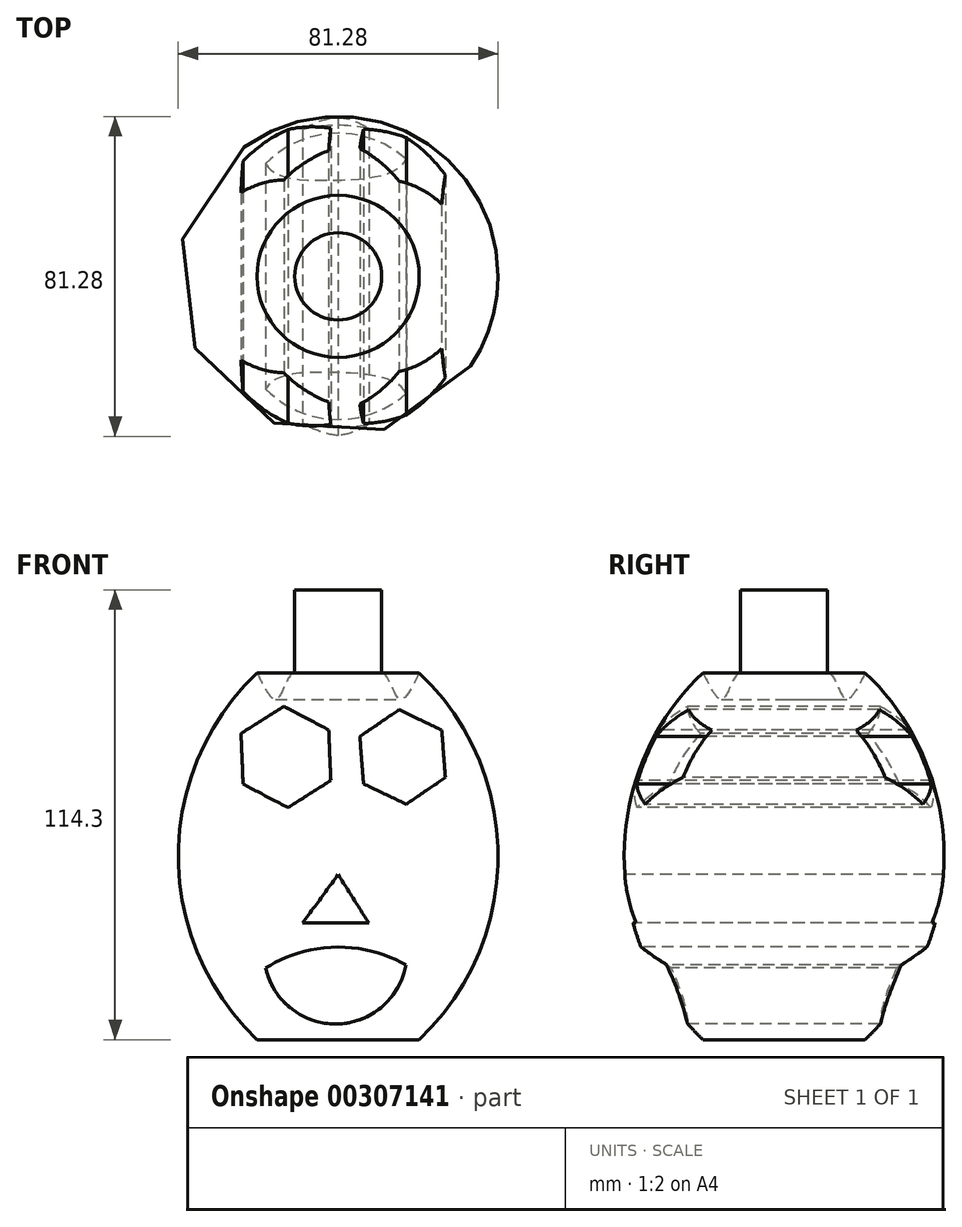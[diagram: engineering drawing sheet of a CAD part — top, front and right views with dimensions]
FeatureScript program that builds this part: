
annotation { "Feature Type Name" : "Feature", "Feature Type Description" : "" }
export const myFeature = defineFeature(function(context is Context, id is Id, definition is map)
    precondition{}
    {
        {
            var Q0;
            Q0=qCreatedBy(makeId("Front.planeOp"),FACE);
            var sketch = newSketch(context, id + "F0", { "sketchPlane" : qUnion([Q0])});
            skLineSegment(sketch, "E0", {"start": v(0, 0) * mm, "end": v(20.6, 0) * mm});
            skArc(sketch, "E1", {"start": v(20.6, 0) * mm, "mid": v(40.64, 46.6) * mm, "end": v(20.6, 93.21) * mm});
            skFitSpline(sketch, "E2", {"points": [v(20.6, 93.21) * mm, v(15.47, 86.64) * mm, v(11.1, 93.21) * mm, v(3.47, 86.37) * mm, v(0, 89.37) * mm], "startDerivative": vector(-21.04, -43.12) * mm, "endDerivative": vector(-15.42, 27.86) * mm});
            skLineSegment(sketch, "E3", {"start": v(0, 89.37) * mm, "end": v(0, 0) * mm});
            skSolve(sketch);
        }
        {
            var Q0;
            Q0 = qSketchRegion(id + "F0", true);
            var Q1;
            Q1=sQuery(id+"F0.wireOp",EDGE,"E3");
            revolve(context, id + "F1", {"entities" : qUnion([Q0]), "axis" : qUnion([Q1]), "revolveType" : RevolveType.FULL});
        }
        {
            var Q0;
            Q0=qCreatedBy(makeId("Top.planeOp"),FACE);
            var sketch = newSketch(context, id + "F2", { "sketchPlane" : qUnion([Q0])});
            skCircle(sketch, "E4", {"center": v(0, 0) * mm, "radius": 11.08 * mm});
            skSolve(sketch);
        }
        {
            var Q0;
            Q0 = qSketchRegion(id + "F2", true);
            extrude(context, id + "F3", {"entities" : qUnion([Q0]), "operationType" : NewBodyOperationType.ADD, "depth" : 114.3 * mm});
        }
        {
            var Q0;
            Q0=qCreatedBy(makeId("Front.planeOp"),FACE);
            var sketch = newSketch(context, id + "F4", { "sketchPlane" : qUnion([Q0])});
            skPoint(sketch, "E5.0.midPoint", {"position": v(-19.24, 81.24) * mm});
            skCircle(sketch, "E6.cCircle", {"center": v(16.37, 71.82) * mm, "radius": 10.44 * mm, "construction": true});
            skLineSegment(sketch, "E6.0", {"start": v(15.44, 83.84) * mm, "end": v(26.31, 78.64) * mm});
            skLineSegment(sketch, "E6.1", {"start": v(26.31, 78.64) * mm, "end": v(27.25, 66.62) * mm});
            skLineSegment(sketch, "E6.2", {"start": v(27.25, 66.62) * mm, "end": v(17.3, 59.8) * mm});
            skLineSegment(sketch, "E6.3", {"start": v(17.3, 59.8) * mm, "end": v(6.44, 65) * mm});
            skLineSegment(sketch, "E6.4", {"start": v(6.44, 65) * mm, "end": v(5.5, 77.02) * mm});
            skLineSegment(sketch, "E6.5", {"start": v(5.5, 77.02) * mm, "end": v(15.44, 83.84) * mm});
            skPoint(sketch, "E6.0.midPoint", {"position": v(20.88, 81.24) * mm});
            skLineSegment(sketch, "E7", {"start": v(0, 41.94) * mm, "end": v(7.78, 29.66) * mm});
            skLineSegment(sketch, "E8", {"start": v(7.78, 29.66) * mm, "end": v(-9, 29.66) * mm});
            skLineSegment(sketch, "E9", {"start": v(-9, 29.66) * mm, "end": v(0, 41.94) * mm});
            skArc(sketch, "E10", {"start": v(17.2, 19.01) * mm, "mid": v(-0.73, 23.52) * mm, "end": v(-18.42, 18.2) * mm});
            skArc(sketch, "E11", {"start": v(-18.42, 18.2) * mm, "mid": v(-0.28, 3.99) * mm, "end": v(17.2, 19.01) * mm});
            skCircle(sketch, "E12.cCircle", {"center": v(-13.28, 71.82) * mm, "radius": 11.15 * mm, "construction": true});
            skLineSegment(sketch, "E12.0", {"start": v(-24.68, 77.8) * mm, "end": v(-13.8, 84.68) * mm});
            skLineSegment(sketch, "E12.1", {"start": v(-13.8, 84.68) * mm, "end": v(-2.4, 78.71) * mm});
            skLineSegment(sketch, "E12.2", {"start": v(-2.4, 78.71) * mm, "end": v(-1.87, 65.85) * mm});
            skLineSegment(sketch, "E12.3", {"start": v(-1.87, 65.85) * mm, "end": v(-12.75, 58.96) * mm});
            skLineSegment(sketch, "E12.4", {"start": v(-12.75, 58.96) * mm, "end": v(-24.15, 64.93) * mm});
            skLineSegment(sketch, "E12.5", {"start": v(-24.15, 64.93) * mm, "end": v(-24.68, 77.8) * mm});
            skSolve(sketch);
        }
        {
            var Q0;
            Q0 = qSketchRegion(id + "F4", true);
            extrude(context, id + "F5", {"entities" : qUnion([Q0]), "operationType" : NewBodyOperationType.REMOVE, "endBound" : BoundingType.SYMMETRIC, "oppositeDirection" : true, "depth" : 939.8 * mm});
        }
    });
